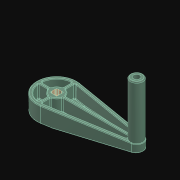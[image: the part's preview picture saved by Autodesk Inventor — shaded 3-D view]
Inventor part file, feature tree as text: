
AUTODESK INVENTOR PART (.ipt)
format: ipt  version: 2021.3 (Build 253353010, 353A)  size: 722,944 bytes
history: native  units: in
note: dims shown in document units (in); Inventor stores cm internally (conversion verified against a paired STEP export)
features: sketch x1, other x1, imported_body x1, extrude x1
ambient origin geometry x8: Origin, YZ Plane, XZ Plane, XY Plane, X Axis, Y Axis, Z Axis, Center Point
bodies: Solid1 (feature_tree)
feature tree (4):
  sketch  "Sketch1"  dims[d0=0.3937in d1=0.0in]
  other  "Srf1"
  imported_body  "Imported1"
  extrude  "ExtrusionSrf1"  [1 undecoded]
note: 1 required parameter value undecoded (feature->parameter linkage not recoverable at this tier; creation-order binding heuristic only, values carry confidence <= 0.55)
